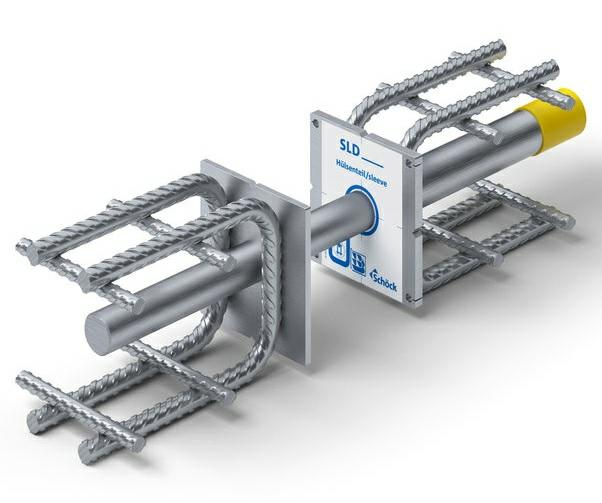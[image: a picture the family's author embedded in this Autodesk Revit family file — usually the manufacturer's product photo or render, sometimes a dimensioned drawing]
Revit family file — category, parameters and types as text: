
# Revit family: r2016_en_v1_schoeck_dorn
name_source: partatom
category: Обобщенные модели
revit_build: Autodesk Revit 2016 (Build: 20150714_1515(x64)
units: mm (PartAtom-declared; Revit-internal decimal feet)

## family parameters
Всегда вертикально = Да
Может служить основой для арматурных стержней = Нет
На основе рабочей плоскости = Нет
Общий = Нет
При загрузке вырезать с полостями = Нет
Размер круглого соединителя = Использовать диаметр
Тип детали = Нормальный
Точка расчета площади = Нет

## types (14) — shared parameters
Lookup Table Name1 = SchoeckCode
Lookup Table Name2 = SchoeckDorn
Lookup Table Name4 = SchoeckType
Material = Stell
Material_Fire protection collar = Fire protection collar
Producer = Schöck
URL = http://www.schoeck.com
Unit = Each
Изготовитель = Schöck

## per-type parameters (varying)
| type | Mass | Name | PartNumber | Product number |
| SLD 60 | 7.178 | Schoeck Dorn SLD 60 | 902005 | 902005 |
| SLD Q 60 | 13.584 | Schoeck Dorn SLD Q 60 | 902012 | 902012 |
| SLD 40 | 2.548 | Schoeck Dorn SLD 40 | 902003 | 902003 |
| SLD Q 40 | 2.756 | Schoeck Dorn SLD Q 40 | 902010 | 902010 |
| SLD 50 | 3.658 | Schoeck Dorn SLD 50 | 902004 | 902004 |
| SLD Q 50 | 4.961 | Schoeck Dorn SLD Q 50 | 902011 | 902011 |
| SLD 70 | 22.133 | Schoeck Dorn SLD 70 | 902006 | 902006 |
| SLD 80 | 3.751 | Schoeck Dorn SLD 80 | 902007 | 902007 |
| SLD Q 70 | 3.154 | Schoeck Dorn SLD Q 70 | 902013 | 902013 |
| SLD Q 80 | 4.721 | Schoeck Dorn SLD Q 80 | 902014 | 902014 |
| SLD 120 | 6.416 | Schoeck Dorn SLD 120 | 902008 | 902008 |
| SLD Q 120 | 10.163 | Schoeck Dorn SLD Q 120 | 902015 | 902015 |
| SLD Q 150 | 31.674 | Schoeck Dorn SLD Q 150 | 902016 | 902016 |
| SLD 150 | 18.984 | Schoeck Dorn SLD 150 | 902009 | 902009 |

note: column(s) folded — value = type name in every type: Identification, Lookup Table Name3

## geometry (parser evidence)
native form markers: Blend x2
no freeform markers — native parametric forms only
